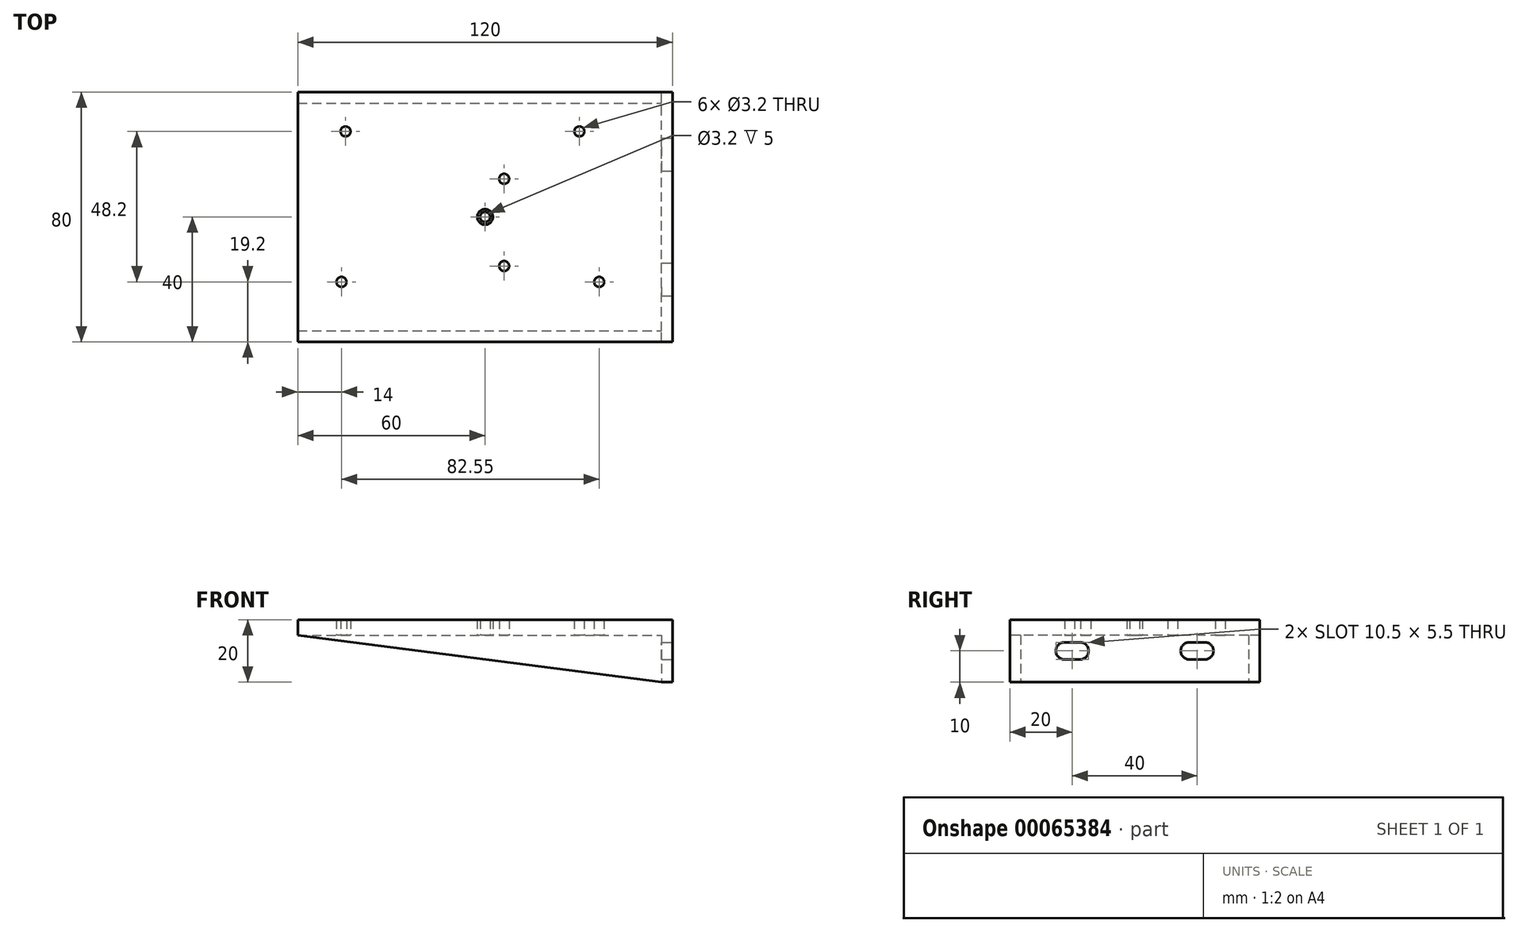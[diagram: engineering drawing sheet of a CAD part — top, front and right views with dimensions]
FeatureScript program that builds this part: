
annotation { "Feature Type Name" : "Feature", "Feature Type Description" : "" }
export const myFeature = defineFeature(function(context is Context, id is Id, definition is map)
    precondition{}
    {
        {
            var Q0;
            Q0=qCreatedBy(makeId("Top.planeOp"),FACE);
            var sketch = newSketch(context, id + "F0", { "sketchPlane" : qUnion([Q0])});
            skLineSegment(sketch, "E0.bottom", {"start": v(-60, 40) * mm, "end": v(60, 40) * mm});
            skLineSegment(sketch, "E0.top", {"start": v(-60, -40) * mm, "end": v(60, -40) * mm});
            skLineSegment(sketch, "E0.left", {"start": v(-60, 40) * mm, "end": v(-60, -40) * mm});
            skLineSegment(sketch, "E0.right", {"start": v(60, 40) * mm, "end": v(60, -40) * mm});
            skLineSegment(sketch, "E1", {"start": v(-60, 40) * mm, "end": v(60, -40) * mm, "construction": true});
            skLineSegment(sketch, "E2", {"start": v(-60, -40) * mm, "end": v(60, 40) * mm, "construction": true});
            skCircle(sketch, "E3", {"center": v(-46, -20.8) * mm, "radius": 1.6 * mm});
            skCircle(sketch, "E4", {"center": v(-44.7, 27.4) * mm, "radius": 1.6 * mm});
            skCircle(sketch, "E5", {"center": v(6.1, -15.7) * mm, "radius": 1.6 * mm});
            skCircle(sketch, "E6", {"center": v(6.1, 12.2) * mm, "radius": 1.6 * mm});
            skCircle(sketch, "E7", {"center": v(30.2, 27.4) * mm, "radius": 1.6 * mm});
            skCircle(sketch, "E8", {"center": v(36.55, -20.8) * mm, "radius": 1.6 * mm});
            skLineSegment(sketch, "E9", {"start": v(-46, 27.4) * mm, "end": v(-46, -20.8) * mm, "construction": true});
            skLineSegment(sketch, "E10", {"start": v(-44.7, 27.4) * mm, "end": v(-44.7, -20.8) * mm, "construction": true});
            skLineSegment(sketch, "E11", {"start": v(6.1, 27.4) * mm, "end": v(6.1, -20.8) * mm, "construction": true});
            skLineSegment(sketch, "E12", {"start": v(30.2, 27.4) * mm, "end": v(30.2, -20.8) * mm, "construction": true});
            skLineSegment(sketch, "E13", {"start": v(36.55, 27.4) * mm, "end": v(36.55, -20.8) * mm, "construction": true});
            skLineSegment(sketch, "E14", {"start": v(-46, -20.8) * mm, "end": v(36.55, -20.8) * mm, "construction": true});
            skLineSegment(sketch, "E15", {"start": v(-46, -15.7) * mm, "end": v(36.55, -15.7) * mm, "construction": true});
            skLineSegment(sketch, "E16", {"start": v(-46, 12.2) * mm, "end": v(36.55, 12.2) * mm, "construction": true});
            skLineSegment(sketch, "E17", {"start": v(-46, 27.4) * mm, "end": v(36.55, 27.4) * mm, "construction": true});
            skLineSegment(sketch, "E18.bottom", {"start": v(-60, 30) * mm, "end": v(41.6, 30) * mm, "construction": true});
            skLineSegment(sketch, "E18.top", {"start": v(-60, -23.3) * mm, "end": v(41.6, -23.3) * mm, "construction": true});
            skLineSegment(sketch, "E18.left", {"start": v(-60, 30) * mm, "end": v(-60, -23.3) * mm, "construction": true});
            skLineSegment(sketch, "E18.right", {"start": v(41.6, 30) * mm, "end": v(41.6, -23.3) * mm, "construction": true});
            skSolve(sketch);
        }
        {
            var Q0;
            Q0 = qSketchRegion(id + "F0", true);
            extrude(context, id + "F1", {"entities" : qUnion([Q0]), "depth" : 5 * mm});
        }
        {
            var Q0;
            Q0=makeQuery(id+"F1.opExtrude","SWEPT_FACE",FACE,{"disambiguationData":[OSD([sQuery(id+"F0.wireOp",EDGE,"E0.right")])]});
            var sketch = newSketch(context, id + "F2", { "sketchPlane" : qUnion([Q0])});
            skLineSegment(sketch, "E19.bottom", {"start": v(-40, 5) * mm, "end": v(40, 5) * mm});
            skLineSegment(sketch, "E19.top", {"start": v(-40, -15) * mm, "end": v(40, -15) * mm});
            skLineSegment(sketch, "E19.left", {"start": v(-40, 5) * mm, "end": v(-40, -15) * mm});
            skLineSegment(sketch, "E19.right", {"start": v(40, 5) * mm, "end": v(40, -15) * mm});
            skLineSegment(sketch, "E20", {"start": v(-50.96, -5) * mm, "end": v(50.96, -5) * mm, "construction": true});
            skArc(sketch, "E21", {"start": v(-17.5, -7.75) * mm, "mid": v(-14.75, -5) * mm, "end": v(-17.5, -2.25) * mm});
            skLineSegment(sketch, "E22", {"start": v(-22.5, -2.25) * mm, "end": v(-17.5, -2.25) * mm});
            skLineSegment(sketch, "E23", {"start": v(-22.5, -7.75) * mm, "end": v(-17.5, -7.75) * mm});
            skArc(sketch, "E24.trimOffspring", {"start": v(-22.5, -2.25) * mm, "mid": v(-25.25, -5) * mm, "end": v(-22.5, -7.75) * mm});
            skLineSegment(sketch, "E25", {"start": v(0, 16.25) * mm, "end": v(0, -46.56) * mm, "construction": true});
            skLineSegment(sketch, "E26", {"start": v(-20, 26.15) * mm, "end": v(-20, -64.12) * mm, "construction": true});
            skLineSegment(sketch, "E27.MirrorCS", {"start": v(22.5, -7.75) * mm, "end": v(17.5, -7.75) * mm});
            skLineSegment(sketch, "E28.MirrorCS", {"start": v(22.5, -2.25) * mm, "end": v(17.5, -2.25) * mm});
            skArc(sketch, "E29.MirrorCS", {"start": v(22.5, -2.25) * mm, "mid": v(25.25, -5) * mm, "end": v(22.5, -7.75) * mm});
            skArc(sketch, "E30.MirrorCS", {"start": v(17.5, -7.75) * mm, "mid": v(14.75, -5) * mm, "end": v(17.5, -2.25) * mm});
            skCircle(sketch, "E31", {"center": v(0, -5) * mm, "radius": 4.5 * mm, "construction": true});
            skSolve(sketch);
        }
        {
            var Q0;
            Q0 = qSketchRegion(id + "F2", true);
            extrude(context, id + "F3", {"entities" : qUnion([Q0]), "operationType" : NewBodyOperationType.ADD, "oppositeDirection" : true, "depth" : 3.5 * mm});
        }
        {
            var Q0;
            Q0=makeQuery(id+"F3.boolean.opBoolean","MERGE",FACE,{"derivedFrom":[makeQuery(id+"F1.opExtrude","SWEPT_FACE",FACE,{"disambiguationData":[OSD([sQuery(id+"F0.wireOp",EDGE,"E0.top")])]}),makeQuery(id+"F3.opExtrude","SWEPT_FACE",FACE,{"disambiguationData":[OSD([sQuery(id+"F2.wireOp",EDGE,"E19.left")])]})]});
            var sketch = newSketch(context, id + "F4", { "sketchPlane" : qUnion([Q0])});
            skLineSegment(sketch, "E32", {"start": v(56.5, -15) * mm, "end": v(56.5, 0) * mm});
            skLineSegment(sketch, "E33", {"start": v(56.5, 0) * mm, "end": v(-60, 0) * mm});
            skLineSegment(sketch, "E34", {"start": v(-60, 0) * mm, "end": v(56.5, -15) * mm});
            skSolve(sketch);
        }
        {
            var Q0;
            Q0 = qSketchRegion(id + "F4", true);
            extrude(context, id + "F5", {"entities" : qUnion([Q0]), "operationType" : NewBodyOperationType.ADD, "oppositeDirection" : true, "depth" : 3.5 * mm});
        }
        {
            var Q0;
            Q0=makeQuery(id+"F3.boolean.opBoolean","MERGE",FACE,{"derivedFrom":[makeQuery(id+"F1.opExtrude","SWEPT_FACE",FACE,{"disambiguationData":[OSD([sQuery(id+"F0.wireOp",EDGE,"E0.bottom")])]}),makeQuery(id+"F3.opExtrude","SWEPT_FACE",FACE,{"disambiguationData":[OSD([sQuery(id+"F2.wireOp",EDGE,"E19.right")])]})]});
            var sketch = newSketch(context, id + "F6", { "sketchPlane" : qUnion([Q0])});
            skLineSegment(sketch, "E35", {"start": v(-56.5, -15) * mm, "end": v(-56.5, 0) * mm});
            skLineSegment(sketch, "E36", {"start": v(-56.5, 0) * mm, "end": v(60, 0) * mm});
            skLineSegment(sketch, "E37", {"start": v(60, 0) * mm, "end": v(-56.5, -15) * mm});
            skSolve(sketch);
        }
        {
            var Q0;
            Q0 = qSketchRegion(id + "F6", true);
            extrude(context, id + "F7", {"entities" : qUnion([Q0]), "operationType" : NewBodyOperationType.ADD, "oppositeDirection" : true, "depth" : 3.5 * mm});
        }
        {
            var Q0;
            Q0=qCreatedBy(makeId("Top.planeOp"),FACE);
            var sketch = newSketch(context, id + "F8", { "sketchPlane" : qUnion([Q0])});
            skCircle(sketch, "E38", {"center": v(0, 0) * mm, "radius": 2.5 * mm});
            skCircle(sketch, "E39", {"center": v(0, 0) * mm, "radius": 1.6 * mm});
            skSolve(sketch);
        }
        {
            var Q0;
            Q0 = qSketchRegion(id + "F8", true);
            extrude(context, id + "F9", {"entities" : qUnion([Q0]), "depth" : 5 * mm});
        }
    });
